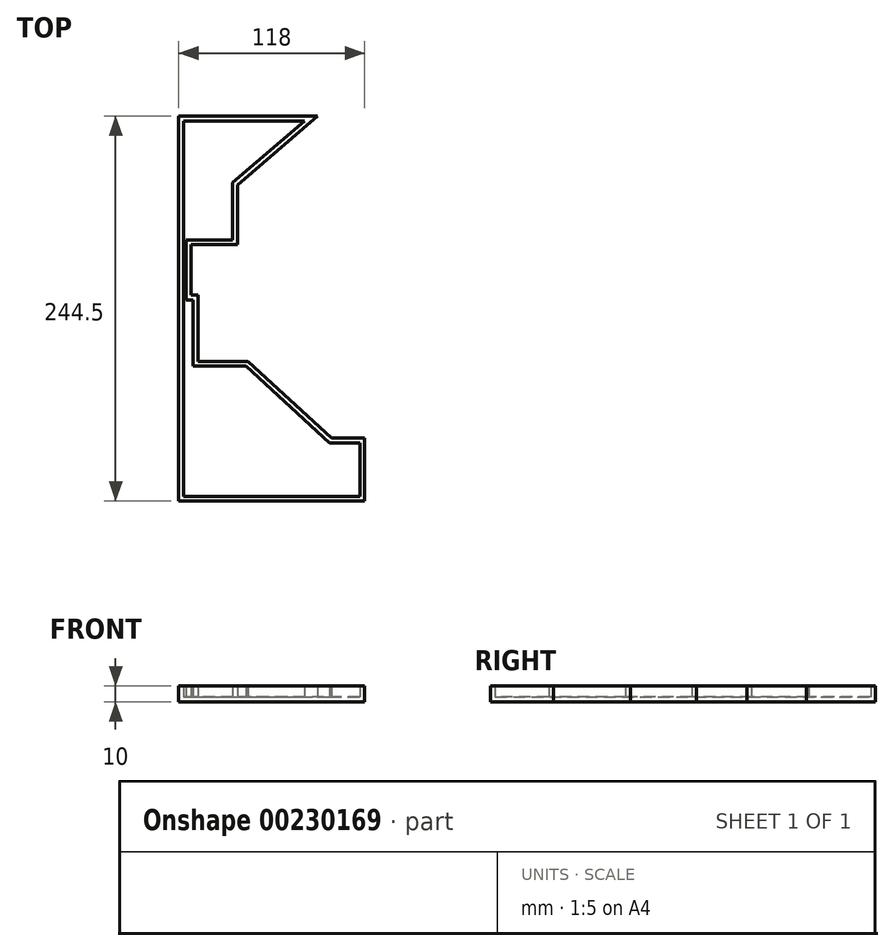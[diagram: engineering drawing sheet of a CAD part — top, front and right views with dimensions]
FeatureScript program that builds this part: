
annotation { "Feature Type Name" : "Feature", "Feature Type Description" : "" }
export const myFeature = defineFeature(function(context is Context, id is Id, definition is map)
    precondition{}
    {
        {
            var Q0;
            Q0=qCreatedBy(makeId("Top.planeOp"),FACE);
            var sketch = newSketch(context, id + "F0", { "sketchPlane" : qUnion([Q0])});
            skLineSegment(sketch, "E0", {"start": v(4.72, 155.62) * mm, "end": v(92.72, 155.62) * mm});
            skLineSegment(sketch, "E1", {"start": v(92.72, 155.62) * mm, "end": v(41.94, 111.91) * mm});
            skLineSegment(sketch, "E2", {"start": v(41.94, 111.91) * mm, "end": v(41.94, 73.91) * mm});
            skLineSegment(sketch, "E3", {"start": v(41.94, 73.91) * mm, "end": v(12.44, 73.91) * mm});
            skLineSegment(sketch, "E4", {"start": v(12.44, 73.91) * mm, "end": v(12.44, 41.91) * mm});
            skLineSegment(sketch, "E5", {"start": v(12.44, 41.91) * mm, "end": v(16.94, 41.91) * mm});
            skLineSegment(sketch, "E6", {"start": v(16.94, 41.91) * mm, "end": v(16.94, -0.09) * mm});
            skLineSegment(sketch, "E7", {"start": v(16.94, -0.09) * mm, "end": v(48.78, -0.09) * mm});
            skLineSegment(sketch, "E8", {"start": v(48.78, -0.09) * mm, "end": v(101.72, -48.88) * mm});
            skLineSegment(sketch, "E9", {"start": v(122.72, -88.88) * mm, "end": v(4.72, -88.88) * mm});
            skLineSegment(sketch, "E10", {"start": v(4.72, -88.88) * mm, "end": v(4.72, 155.62) * mm});
            skLineSegment(sketch, "E11", {"start": v(101.72, -48.88) * mm, "end": v(122.72, -48.88) * mm});
            skLineSegment(sketch, "E12", {"start": v(122.72, -48.88) * mm, "end": v(122.72, -88.88) * mm});
            skLineSegment(sketch, "E13", {"start": v(122.72, -88.88) * mm, "end": v(122.72, -88.88) * mm});
            skLineSegment(sketch, "E14", {"start": v(0, 155.62) * mm, "end": v(0, 0) * mm});
            skSolve(sketch);
        }
        {
            var Q0;
            Q0=makeQuery(id+"F0.imprint","IMPRINT",FACE,{"disambiguationData":[TD([[makeQuery(id+"F0.imprint","IMPRINT",EDGE,{"derivedFrom":sQuery(id+"F0.wireOp",EDGE,"E0")}),-1.0]])]});
            extrude(context, id + "F1", {"entities" : qUnion([Q0]), "depth" : 10 * mm});
        }
        {
            var Q0;
            Q0=makeQuery(id+"F1.opExtrude","CAP_FACE",FACE,{"disambiguationData":[OSD([sQuery(id+"F0.wireOp",EDGE,"E0"),sQuery(id+"F0.wireOp",EDGE,"E1"),sQuery(id+"F0.wireOp",EDGE,"E2"),sQuery(id+"F0.wireOp",EDGE,"E3"),sQuery(id+"F0.wireOp",EDGE,"E4"),sQuery(id+"F0.wireOp",EDGE,"E5"),sQuery(id+"F0.wireOp",EDGE,"E6"),sQuery(id+"F0.wireOp",EDGE,"E7"),sQuery(id+"F0.wireOp",EDGE,"E8"),sQuery(id+"F0.wireOp",EDGE,"E9"),sQuery(id+"F0.wireOp",EDGE,"E10"),sQuery(id+"F0.wireOp",EDGE,"E11"),sQuery(id+"F0.wireOp",EDGE,"E12")])],"isStart":false});
            shell(context, id + "F2", {"entities" : qUnion([Q0]), "thickness" : 3 * mm});
        }
    });
